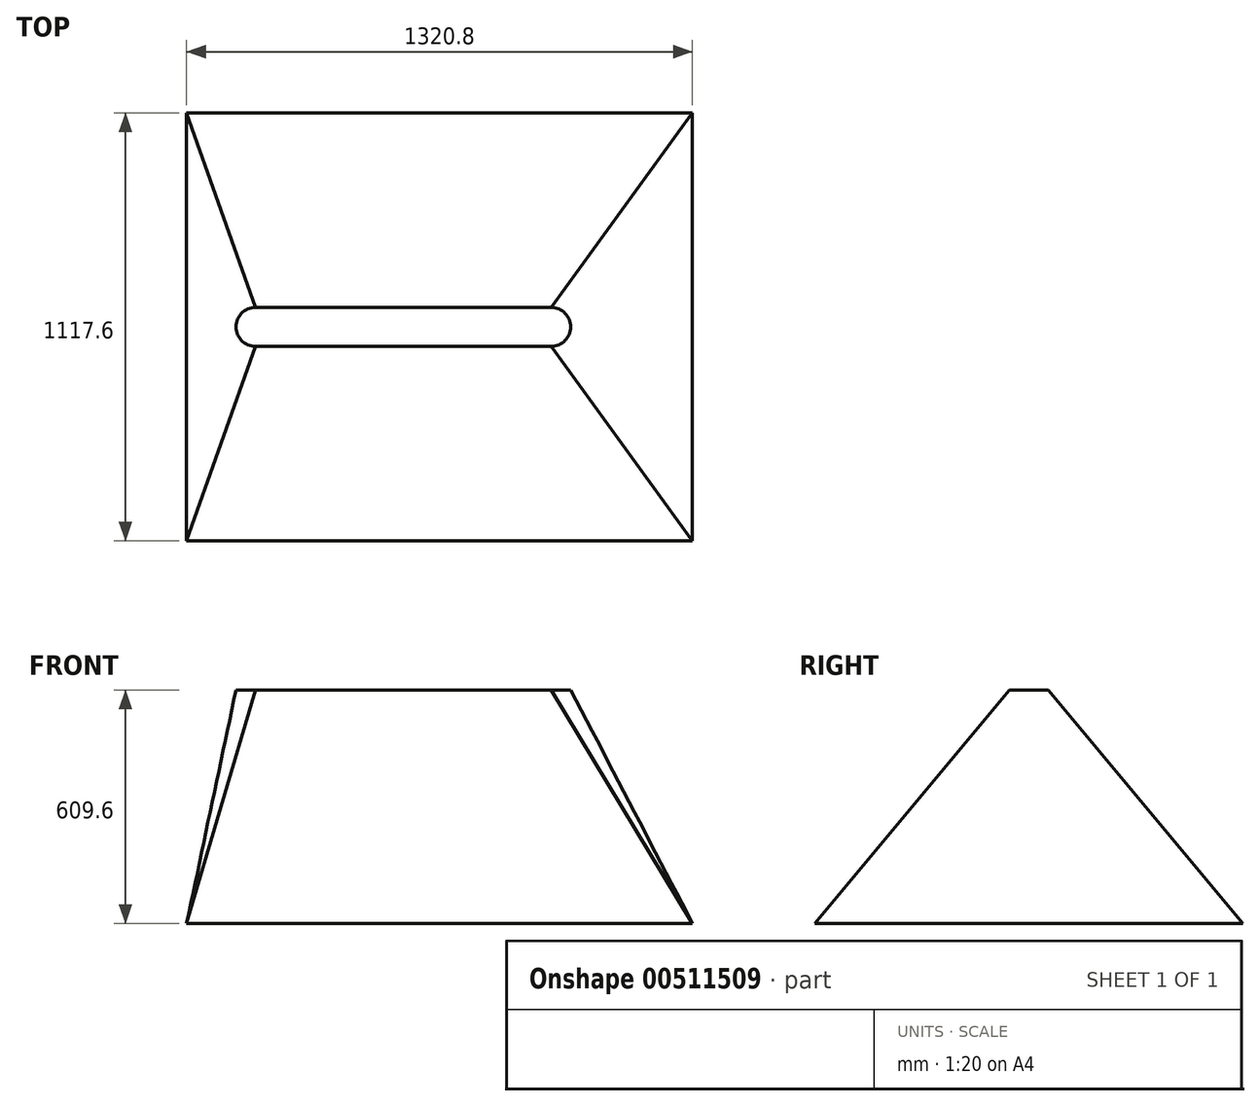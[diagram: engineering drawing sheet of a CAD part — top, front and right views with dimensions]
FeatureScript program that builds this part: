
annotation { "Feature Type Name" : "Feature", "Feature Type Description" : "" }
export const myFeature = defineFeature(function(context is Context, id is Id, definition is map)
    precondition{}
    {
        {
            var Q0;
            Q0=qCreatedBy(makeId("Top.planeOp"),FACE);
            cPlane(context, id + "F0", {"entities" : qUnion([Q0]), "cplaneType" : CPlaneType.OFFSET, "offset" : 609.6 * mm, "width" : 152.4 * mm, "height" : 152.4 * mm});
        }
        {
            var Q0;
            Q0=qCreatedBy(makeId("Top.planeOp"),FACE);
            var sketch = newSketch(context, id + "F1", { "sketchPlane" : qUnion([Q0])});
            skLineSegment(sketch, "E0.bottom", {"start": v(-660.4, -558.8) * mm, "end": v(660.4, -558.8) * mm});
            skLineSegment(sketch, "E0.top", {"start": v(-660.4, 558.8) * mm, "end": v(660.4, 558.8) * mm});
            skLineSegment(sketch, "E1", {"start": v(-660.4, 558.8) * mm, "end": v(-660.4, -558.8) * mm});
            skLineSegment(sketch, "E2", {"start": v(660.4, 558.8) * mm, "end": v(660.4, -558.8) * mm});
            skSolve(sketch);
        }
        {
            var Q0;
            Q0=qCreatedBy(id+"F0.planeOp",FACE);
            var sketch = newSketch(context, id + "F2", { "sketchPlane" : qUnion([Q0])});
            skLineSegment(sketch, "E3.bottom", {"start": v(-480.94, 50.8) * mm, "end": v(291.77, 50.8) * mm});
            skLineSegment(sketch, "E3.top", {"start": v(-480.94, -50.8) * mm, "end": v(291.77, -50.8) * mm});
            skArc(sketch, "E4", {"start": v(-480.94, 50.8) * mm, "mid": v(-531.74, 0) * mm, "end": v(-480.94, -50.8) * mm});
            skArc(sketch, "E5", {"start": v(291.77, -50.8) * mm, "mid": v(342.57, 0) * mm, "end": v(291.77, 50.8) * mm});
            skSolve(sketch);
        }
        {
            var Q0;
            Q0=makeQuery(id+"F1.imprint","IMPRINT",FACE,{"disambiguationData":[TD([[makeQuery(id+"F1.imprint","IMPRINT",EDGE,{"derivedFrom":sQuery(id+"F1.wireOp",EDGE,"E0.bottom")}),1.0]])]});
            var Q1;
            Q1=makeQuery(id+"F2.imprint","IMPRINT",FACE,{"disambiguationData":[TD([[makeQuery(id+"F2.imprint","IMPRINT",EDGE,{"derivedFrom":sQuery(id+"F2.wireOp",EDGE,"E3.bottom")}),-1.0]])]});
            loft(context, id + "F3", {"sheetProfilesArray" : [{ "sheetProfileEntities" : qUnion([Q0]) }, { "sheetProfileEntities" : qUnion([Q1]) }]});
        }
    });
